# Revit family: Legrand Mini Colonnes universelles
name_source: partatom
category: Installations électriques
units: mm (PartAtom-declared; Revit-internal decimal feet)

## family parameters
Basée sur le plan de construction = Non
Conserver l'orientation des annotations = Non
Cote de connecteur circulaire = Utiliser le diamètre
Couper avec des vides une fois chargée = Non
Partagée = Non
Point de calcul de pièce = Non
Toujours verticalement = Oui
Type d'élément = Normal

## types (8) — shared parameters
Fabricant = LEGRAND
Largeur = 75 mm
Matériau principal = Aluminium
Standard = Universelle
Séparateur = 35 mm
zero-valued in all types: Elévation par défaut

## per-type parameters (varying)
| type | 1 CPT | 2 CPT | Black | Column stand | Description | Finition | H1 | HC | Longueur | Matériau couvercle | Matériaux corps | Modèle | Nombre de compartiments |
| Colonnette 1 cpt 80 0,3M Blanc | Oui | Non | Non | Pied mobile : Pied pour Colonnettes Blanc | Colonnette universelle 1 compartiment 0,3m Blanc | Blanc | 300 mm | 260 mm  [stored 0.853018 ft] | 82 mm | Legrand - Plastique blanc | Legrand - Aluminium blanc | LG-653100 | 1 compartiment |
| Colonnette 1 cpt 80 0,68M Blanc | Oui | Non | Non | Pied mobile : Pied pour Colonnettes Blanc | Colonnette universelle 1 compartiment 0,68m Blanc | Blanc | 680 mm  [stored 2.23097 ft] | 640 mm  [stored 2.09974 ft] | 82 mm | Legrand - Plastique blanc | Legrand - Aluminium blanc | LG-653103 | 1 compartiment |
| Colonnette 2 cpts 80 0,30M BL | Non | Oui | Non | Pied mobile : Pied pour Colonnettes Blanc | Colonnette universelle 2 compartiments 0,30m Blanc | Blanc | 300 mm | 260 mm  [stored 0.853018 ft] | 125 mm | Legrand - Plastique blanc | Legrand - Aluminium blanc | LG-653120 | 2 compartiments |
| Colonnette 2 cpts 80 0,68M BL | Non | Oui | Non | Pied mobile : Pied pour Colonnettes Blanc | Colonnette universelle 2 compartiments 0,68m Blanc | Blanc | 680 mm  [stored 2.23097 ft] | 640 mm  [stored 2.09974 ft] | 125 mm | Legrand - Plastique blanc | Legrand - Aluminium blanc | LG-653123 | 2 compartiments |
| Colonnette 1 cpt 80 0,68M Noir | Oui | Non | Oui | Tablette : Table pour Colonnettes T1/2 | Colonnette universelle 1 compartiment 0,68m Noir | Noir | 680 mm  [stored 2.23097 ft] | 640 mm  [stored 2.09974 ft] | 82 mm | Legrand - Plastique noir | Legrand - Aluminium noir | LG-653105 | 1 compartiment |
| Colonnette 1 cpt 80 0,3M Noir | Oui | Non | Oui | Tablette : Table pour Colonnettes T1/2 | Colonnette universelle 1 compartiment 0,3m Noir | Noir | 300 mm | 260 mm  [stored 0.853018 ft] | 82 mm | Legrand - Plastique noir | Legrand - Aluminium noir | LG-653102 | 1 compartiment |
| Colonnette 2 cpt 80 0,30M Noir | Oui | Oui | Non | Tablette : Table pour Colonnettes T1/2 | Colonnette universelle 2 compartiments 0,30m Noir | Noir | 300 mm | 260 mm  [stored 0.853018 ft] | 82 mm | Legrand - Plastique noir | Legrand - Aluminium noir | LG-653122 | 2 compartiments |
| Colonnette 2 cpt 80 0,68M Noir | Non | Oui | Oui | Tablette : Table pour Colonnettes T1/2 | Colonnette universelle 2 compartiments 0,68m Noir | Noir | 680 mm  [stored 2.23097 ft] | 640 mm  [stored 2.09974 ft] | 125 mm | Legrand - Plastique noir | Legrand - Aluminium noir | LG-653125 | 2 compartiments |

note: [stored X ft] marks values corroborated as IEEE doubles in the binary element streams (Revit-internal decimal feet)
